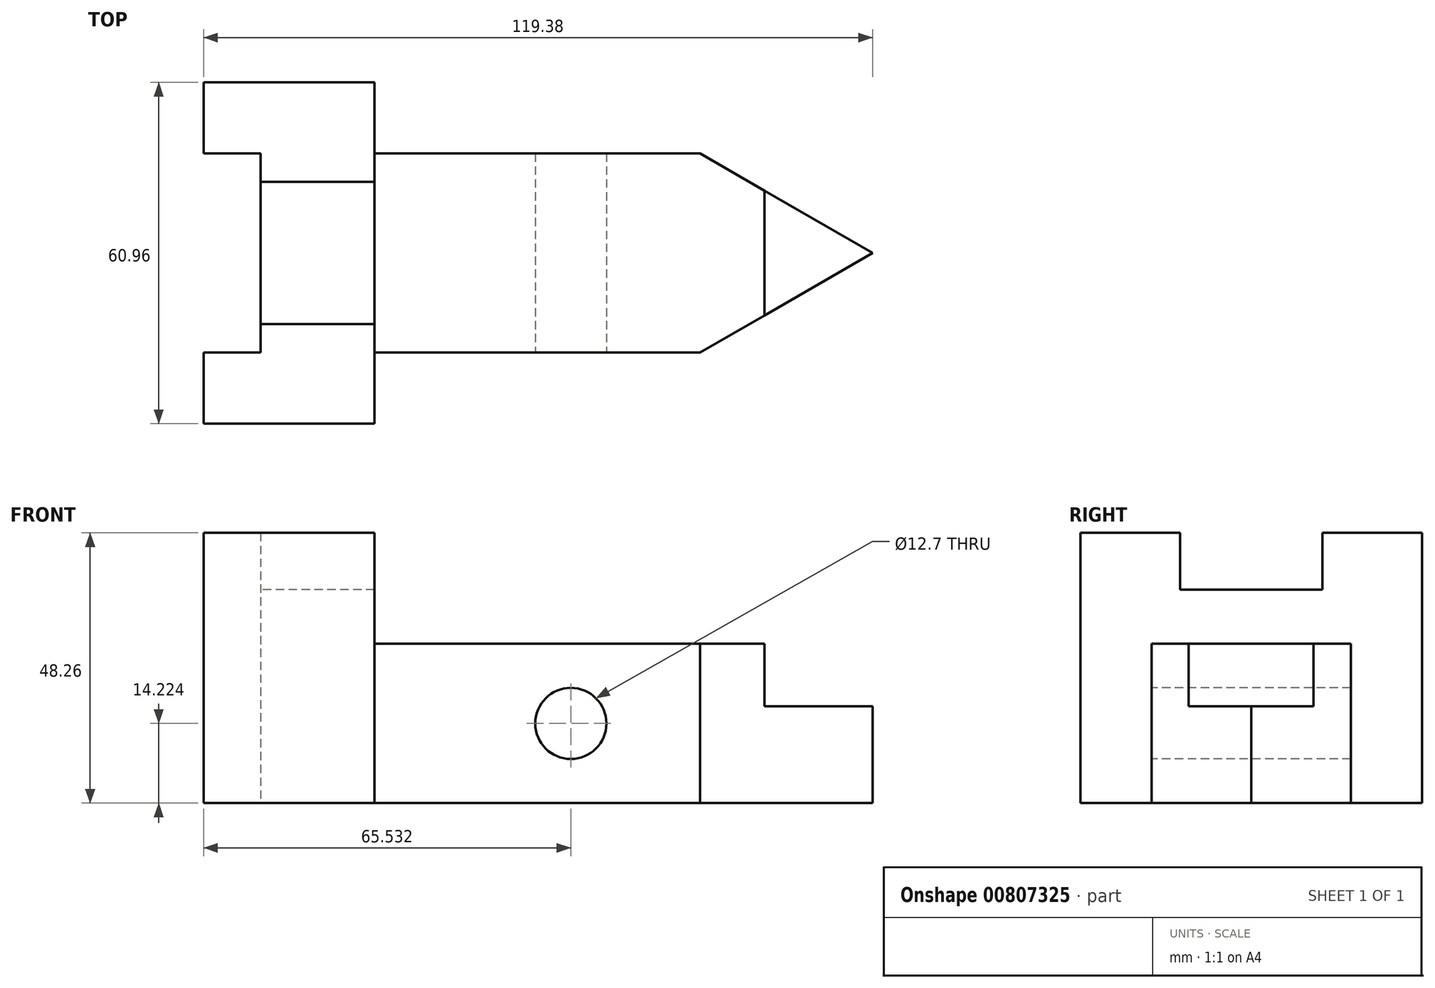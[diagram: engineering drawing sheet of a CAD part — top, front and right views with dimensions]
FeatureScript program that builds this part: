
annotation { "Feature Type Name" : "Feature", "Feature Type Description" : "" }
export const myFeature = defineFeature(function(context is Context, id is Id, definition is map)
    precondition{}
    {
        {
            var Q0;
            Q0=qCreatedBy(makeId("Top.planeOp"),FACE);
            var sketch = newSketch(context, id + "F0", { "sketchPlane" : qUnion([Q0])});
            skLineSegment(sketch, "E0", {"start": v(0, 0) * mm, "end": v(30.48, 0) * mm});
            skLineSegment(sketch, "E1", {"start": v(30.48, 0) * mm, "end": v(30.48, 60.96) * mm});
            skLineSegment(sketch, "E2", {"start": v(30.48, 60.96) * mm, "end": v(0, 60.96) * mm});
            skLineSegment(sketch, "E3", {"start": v(0, 60.96) * mm, "end": v(0, 48.26) * mm});
            skLineSegment(sketch, "E4", {"start": v(0, 48.26) * mm, "end": v(10.16, 48.26) * mm});
            skLineSegment(sketch, "E5", {"start": v(10.16, 48.26) * mm, "end": v(10.16, 12.7) * mm});
            skLineSegment(sketch, "E6", {"start": v(10.16, 12.7) * mm, "end": v(0, 12.7) * mm});
            skLineSegment(sketch, "E7", {"start": v(0, 12.7) * mm, "end": v(0, 0) * mm});
            skLineSegment(sketch, "E8", {"start": v(30.48, 30.48) * mm, "end": v(119.38, 30.48) * mm, "construction": true});
            skLineSegment(sketch, "E9", {"start": v(88.58, 48.26) * mm, "end": v(30.48, 48.26) * mm});
            skLineSegment(sketch, "E10", {"start": v(88.58, 12.7) * mm, "end": v(30.48, 12.7) * mm});
            skLineSegment(sketch, "E11", {"start": v(88.58, 48.26) * mm, "end": v(119.38, 30.48) * mm});
            skLineSegment(sketch, "E12", {"start": v(88.58, 12.7) * mm, "end": v(119.38, 30.48) * mm});
            skLineSegment(sketch, "E13", {"start": v(100.08, 41.63) * mm, "end": v(100.08, 19.33) * mm});
            skSolve(sketch);
        }
        {
            var Q0;
            {var subQ4=sQuery(id+"F0.wireOp",EDGE,"E0");Q0=makeQuery(id+"F0.imprint","IMPRINT",FACE,{"disambiguationData":[TD([[makeQuery(id+"F0.imprint","IMPRINT",EDGE,{"derivedFrom":subQ4}),1.0]])]});}
            extrude(context, id + "F1", {"entities" : qUnion([Q0]), "depth" : 48.26 * mm, "offsetDistance" : 25.4 * mm});
        }
        {
            var Q0;
            {var subQ1=sQuery(id+"F0.wireOp",EDGE,"E9");Q0=makeQuery(id+"F0.imprint","IMPRINT",FACE,{"disambiguationData":[TD([[makeQuery(id+"F0.imprint","IMPRINT",EDGE,{"derivedFrom":subQ1}),1.0]])]});}
            extrude(context, id + "F2", {"entities" : qUnion([Q0]), "operationType" : NewBodyOperationType.ADD, "depth" : 28.45 * mm, "offsetDistance" : 25.4 * mm});
        }
        {
            var Q0;
            {var subQ3=sQuery(id+"F0.wireOp",EDGE,"E13");Q0=makeQuery(id+"F0.imprint","IMPRINT",FACE,{"disambiguationData":[TD([[makeQuery(id+"F0.imprint","IMPRINT",EDGE,{"derivedFrom":subQ3}),1.0]])]});}
            extrude(context, id + "F3", {"entities" : qUnion([Q0]), "operationType" : NewBodyOperationType.ADD, "depth" : 17.27 * mm, "offsetDistance" : 25.4 * mm});
        }
        {
            var Q0;
            Q0=makeQuery(id+"F1.opExtrude","SWEPT_FACE",FACE,{"disambiguationData":[OSD([sQuery(id+"F0.wireOp",EDGE,"E5")])]});
            var sketch = newSketch(context, id + "F4", { "sketchPlane" : qUnion([Q0])});
            skPoint(sketch, "E14.0", {"position": v(0, 48.26) * mm});
            skLineSegment(sketch, "E15.0", {"start": v(-48.26, 48.26) * mm, "end": v(-12.7, 48.26) * mm});
            skPoint(sketch, "E16.0", {"position": v(-60.96, 48.26) * mm});
            skLineSegment(sketch, "E17", {"start": v(-17.78, 48.26) * mm, "end": v(-17.78, 38.1) * mm});
            skLineSegment(sketch, "E18", {"start": v(-17.78, 38.1) * mm, "end": v(-43.18, 38.1) * mm});
            skLineSegment(sketch, "E19", {"start": v(-43.18, 38.1) * mm, "end": v(-43.18, 48.26) * mm});
            skSolve(sketch);
        }
        {
            var Q0;
            {var subQ0=sQuery(id+"F4.wireOp",EDGE,"E17");Q0=makeQuery(id+"F4.imprint","IMPRINT",FACE,{"disambiguationData":[TD([[makeQuery(id+"F4.imprint","IMPRINT",EDGE,{"derivedFrom":subQ0}),-1.0]])]});}
            extrude(context, id + "F5", {"entities" : qUnion([Q0]), "operationType" : NewBodyOperationType.REMOVE, "oppositeDirection" : true, "depth" : 25.4 * mm, "offsetDistance" : 25.4 * mm});
        }
        {
            var Q0;
            Q0=makeQuery(id+"F2.opExtrude","SWEPT_FACE",FACE,{"disambiguationData":[OSD([sQuery(id+"F0.wireOp",EDGE,"E10")])]});
            var sketch = newSketch(context, id + "F6", { "sketchPlane" : qUnion([Q0])});
            skLineSegment(sketch, "E20.0.0", {"start": v(30.48, 0) * mm, "end": v(88.58, 0) * mm});
            skLineSegment(sketch, "E20.0.1", {"start": v(88.58, 0) * mm, "end": v(88.58, 28.45) * mm});
            skLineSegment(sketch, "E20.0.2", {"start": v(88.58, 28.45) * mm, "end": v(30.48, 28.45) * mm});
            skLineSegment(sketch, "E20.0.3", {"start": v(30.48, 28.45) * mm, "end": v(30.48, 0) * mm});
            skCircle(sketch, "E21", {"center": v(65.53, 14.22) * mm, "radius": 6.35 * mm});
            skSolve(sketch);
        }
        {
            var Q0;
            Q0=makeQuery(id+"F6.imprint","IMPRINT",FACE,{"disambiguationData":[TD([[makeQuery(id+"F6.imprint","IMPRINT",EDGE,{"derivedFrom":sQuery(id+"F6.wireOp",EDGE,"E21")}),1.0]])]});
            extrude(context, id + "F7", {"entities" : qUnion([Q0]), "operationType" : NewBodyOperationType.REMOVE, "oppositeDirection" : true, "depth" : 46.48 * mm, "offsetDistance" : 25.4 * mm});
        }
    });
